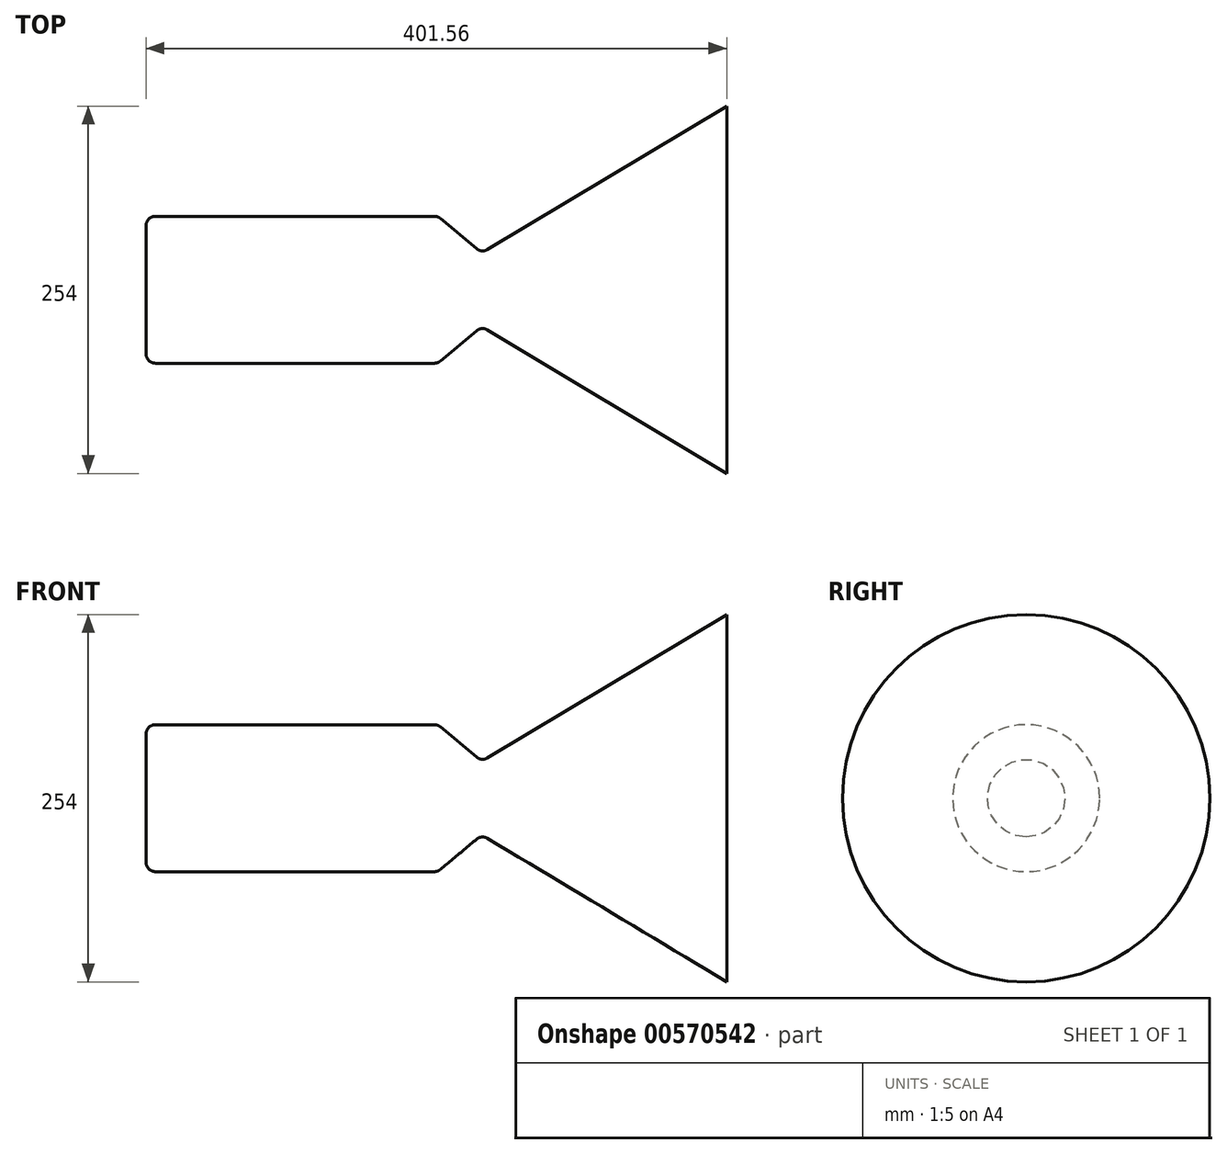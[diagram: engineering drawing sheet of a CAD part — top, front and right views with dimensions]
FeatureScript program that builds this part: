
annotation { "Feature Type Name" : "Feature", "Feature Type Description" : "" }
export const myFeature = defineFeature(function(context is Context, id is Id, definition is map)
    precondition{}
    {
        {
            var Q0;
            Q0=qCreatedBy(makeId("Front.planeOp"),FACE);
            var sketch = newSketch(context, id + "F0", { "sketchPlane" : qUnion([Q0])});
            skLineSegment(sketch, "E0", {"start": v(0, 0) * mm, "end": v(0, 44.45) * mm});
            skLineSegment(sketch, "E1", {"start": v(6.35, 50.8) * mm, "end": v(199.35, 50.8) * mm});
            skLineSegment(sketch, "E2", {"start": v(203.42, 49.32) * mm, "end": v(228.59, 28.3) * mm});
            skLineSegment(sketch, "E3", {"start": v(235.92, 27.72) * mm, "end": v(401.56, 127) * mm});
            skLineSegment(sketch, "E4", {"start": v(401.56, 127) * mm, "end": v(401.56, 0) * mm});
            skLineSegment(sketch, "E5", {"start": v(401.56, 0) * mm, "end": v(0, 0) * mm});
            skPoint(sketch, "E6.visualSharp", {"position": v(232.05, 25.4) * mm});
            skArc(sketch, "E6.filletArc", {"start": v(228.59, 28.3) * mm, "mid": v(232.16, 26.84) * mm, "end": v(235.92, 27.72) * mm});
            skPoint(sketch, "E7.visualSharp", {"position": v(201.65, 50.8) * mm});
            skArc(sketch, "E7.filletArc", {"start": v(203.42, 49.32) * mm, "mid": v(201.51, 50.42) * mm, "end": v(199.35, 50.8) * mm});
            skPoint(sketch, "E8.visualSharp", {"position": v(0, 50.8) * mm});
            skArc(sketch, "E8.filletArc", {"start": v(6.35, 50.8) * mm, "mid": v(1.86, 48.94) * mm, "end": v(0, 44.45) * mm});
            skSolve(sketch);
        }
        {
            var Q0;
            Q0=qSketchRegion(id+"F0",true);
            var Q1;
            Q1=sQuery(id+"F0.wireOp",EDGE,"E5");
            revolve(context, id + "F1", {"entities" : qUnion([Q0]), "axis" : qUnion([Q1]), "revolveType" : RevolveType.FULL});
        }
    });
